# Revit family: VELUX FCM - curb mounted - fixed
name_source: partatom
category: Windows
units: mm (PartAtom-declared; Revit-internal decimal feet)

## family parameters
Always vertical = No
Cut with Voids When Loaded = No
Host = Roof
OmniClass Number = 23.30.30.14
Room Calculation Point = No
Shared = No

## types (14) — shared parameters
Assembly Code = B3020110
Curb (furnished by others) = Curb - By others - Local code compliant
Curb Height (90mm minimum) = 140 mm
Description = Fixed (non-opening) flat roof skylight
Edge of glazing = 22 mm
Flashing (furnished by others) = Flashing - By others - Local code compliant
Frame finish = Aluminum - Lacquered - Kynar 500 top finish - Neutral Gray
Glazing Material = Glass-VELUX-Laminated
Manufacturer = VELUX
Maximum Roof Pitch = 60 degrees
Minimum Roof Pitch = 0 degrees
Model = FCM Flat Roof Skylight
Technical Drawings URL = http://www.velux.com.au
URL = http://www.velux.com.au
VELUX Australia Glazing options = Laminated (04)
VELUX Glazing options URL = http://www.velux.com.au

## per-type parameters (varying)
| type | Height | Rough Height | Rough Width | Throat Height | Throat Width | Type Comments | Width |
| 1430 | 892 mm  [stored 2.92651 ft] | 775 mm | 368 mm | 870 | 460 | Designed for low roof pitch installation with purpose-built flashings | 485 mm  [stored 1.59121 ft] |
| 2222 | 689 mm  [stored 2.2605 ft] | 572 mm | 572 mm | 665 | 665 | Designed for low roof pitch installations with purpose-built flashings | 689 mm  [stored 2.2605 ft] |
| 2230 | 892 mm  [stored 2.92651 ft] | 775 mm | 572 mm | 870 | 665 | Designed for low roof pitch installations with purpose-built flashings | 689 mm  [stored 2.2605 ft] |
| 2234 | 994 mm | 876 mm | 572 mm | 970 | 665 | Designed for low roof pitch installations with purpose-built flashings | 689 mm  [stored 2.2605 ft] |
| 2246 | 1299 mm  [stored 4.26181 ft] | 1181 mm | 572 mm | 1275 | 665 | Designed for low roof pitch installations with purpose-built flashings | 689 mm  [stored 2.2605 ft] |
| 2270 | 1908 mm  [stored 6.25984 ft] | 1791 mm | 572 mm | 1885 | 665 | Designed for low roof pitch installations with purpose-built flashings | 689 mm  [stored 2.2605 ft] |
| 3030 | 892 mm  [stored 2.92651 ft] | 775 mm | 775 mm | 870 | 870 | Designed for low roof pitch installations with purpose-built flashings | 892 mm  [stored 2.92651 ft] |
| 3046 | 1299 mm  [stored 4.26181 ft] | 1181 mm | 775 mm | 1275 | 870 | Designed for low roof pitch installations with purpose-built flashings | 892 mm  [stored 2.92651 ft] |
| 3434 | 994 mm | 876 mm | 876 mm | 970 | 970 | Designed for low roof pitch installations with purpose-built flashings | 994 mm |
| 4646 | 1299 mm  [stored 4.26181 ft] | 1181 mm | 1181 mm | 1275 | 1275 | Designed for low roof pitch installations with purpose-built flashings | 1299 mm  [stored 4.26181 ft] |
| 3446 | 1299 mm  [stored 4.26181 ft] | 1181 mm | 876 mm | 1275 | 970 | Designed for low roof pitch installations with purpose-built flashings | 994 mm |
| 3055 | 1527 mm  [stored 5.00984 ft] | 1410 mm | 775 mm | 1505 | 870 | Designed for low roof pitch installations with purpose-built flashings | 892 mm  [stored 2.92651 ft] |
| 3072 | 1947 mm  [stored 6.3878 ft] | 1829 mm | 775 mm | 1923 | 870 | Designed for low roof pitch installations with purpose-built flashings | 892 mm  [stored 2.92651 ft] |
| 4672 | 1947 mm  [stored 6.3878 ft] | 1829 mm | 1181 mm | 1923 | 1275 | Designed for low roof pitch installations with purpose-built flashings | 1299 mm  [stored 4.26181 ft] |

note: [stored X ft] marks values corroborated as IEEE doubles in the binary element streams (Revit-internal decimal feet)

## geometry (parser evidence)
native form markers: Sweep x1
no freeform markers — native parametric forms only
